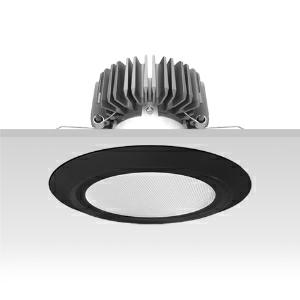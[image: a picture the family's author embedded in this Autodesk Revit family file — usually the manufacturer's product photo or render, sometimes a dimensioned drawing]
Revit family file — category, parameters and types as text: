
# Revit family: 3f_filippi_-_3f_reno_bianco_ampio_3f_filippi_-_30679_a01049_-_3f_reno_200_wh_3000-840_dali_wide___smp_bk_fb56
name_source: partatom
category: Lighting Fixtures
units: mm (PartAtom-declared; Revit-internal decimal feet)

## family parameters
Cut with Voids When Loaded = No
Host = Face
Light Source = No
Part Type = Normal
Room Calculation Point = No
Round Connector Dimension = Use Diameter
Shared = No

## types (1)
- 3F Filippi - 3F Reno Bianco Ampio (1 x LED, 2312 lm, 28 W, 4000 K)
    Apparent Load = 28 VA
    Approval mark = CE
    CIE Flux Codes = 74 92 98 100 100
    Color Rendering = 80
    Color Temperature = 4000 K
    Control Gear = Electronic transformer
    Default Elevation = 1800 mm
    Description = ILLUMINOTECHNICAL
Luminous efficiency 100% (DLOR 100%, ULOR 0%).
Initial luminous flux of the luminaire 2312 lm.
Direct symmetric wide distribution.
Installation Interdistance Transv.D = 1.06 x hu - Long.D = 1.04 x hu.
Tabular UGR (CIE 117 - 4H-8H; S=0.25H; 70/50/20): RUG 22.5 - 22.3.
Beam angle: 70° - 69°.
Luminous efficacy 83 lm/W.
Lifetime (L90/B10): 30000 h. (tq+25°C)
Lifetime (L85/B10): 50000 h. (tq+25°C)
Lifetime (L70/B10): 80000 h. (tq+25°C)
Sudden decreased luminous flux after 50000 hours: 0% (C0).
Photobiological safety in compliance with IEC/TR 62778: RG0 risk exempt, (IEC 62471).
In compliance with IEC/EN 62722-2-1 - IEC/EN 62717 standards.

SOURCE
Compact LED module 3000/840.
Energy efficiency class (UE 2019/2020 - UE 2019/2015): E.
CIE 13.3 Colour rendering index: CRI >80 (R9 <50%).
IES TM-30 Fidelity Index: Rf = 84 Rg = 95.
CCT nominal colour temperature 4000 K.
Colour initial tolerance (MacAdam): SDCM 3.
Zhaga Book 3 compliant.

MECHANICAL
Passive heat dissipator in die-casting aluminium, oversized, for optimum thermal management of the LED module.
Parabolic element with graduated/concentric rings in white polycarbonate.
Transparent external lens with glossy and satin differentiated surfaces, with a cooling and anti-insect system in methacrylate (PMMA).
Fastening spring clips in stainless steel.
Dimensions: diameter 226 mm, height 146 mm. Weight 1.695 kg.
IP44 protection degree for exposed part, IP20 for recessed part.
Mechanical strength to impacts IK05 (0.7 joule).
Glow-wire test resistance 650°C.

ELECTRICAL
Wiring on a separate unit.
Halogen Free DALI-2 DATI (Parts 251, 252, 253), PUSH-DIM, electronic wiring 230V-50/60Hz, power factor 0.97 at full load, THD <25%, constant output current, SELV, class II, 1 driver, 1 DALI addresse.
Power of the luminaire 28 W.
ENEC - CE.
SAFE FLICKER: PstLM=<1 and SVM=<0.4 (IEC TR 61547-1 and IEC TR 63158), to ensure a more comfortable and safe light.
Luminaire compliant with EN 60598-2-22 for power supply from a centralised emergency system CPSS (Central Power Supply System), not incorporated in the luminaire - high risk areas excluded. The default power and flux are 100% in AC and 100% in DC.
Ambient temperature from 0°C to +25°C.
Temperature class T6 max 85°C.
Relative humidity UR: <85%.

INSTALLATION
Pull-up recessed fitting.
False ceiling carving: 200 mm.
All accessories dedicated to this product are available on the Catalog and on our website www.3F-Filippi.com.

ACCESSORIES
A01049 - Anti-glare microprismatic SMP diffuser in methacrylate (PMMA), locked and in line with the trim, in black polycarbonate.

APPLICATIONS
Suitable product for food production plants (HACCP), IFS (Food Version 6), BRC (GSFS Food Version 7).
Environments: architectural, commercial, exhibition areas, transit areas, corridors, shops, display windows, service areas.
In false ceilings with narrow voids.

LIGHT MANAGEMENT
Recommended minimum setting: 10%.
The luminaire, equipped with (DALI-2 DATI) driver, can be controlled manually with 3F Easy Dim technology or automatically/manually with wired or wireless DALI/D2D control systems.
The D2D driver guarantees interoperability with other devices with the same certification by making the following information available:
Device Data (Part 251), Energy Report (Part 252), Diagnosis & Maintenance (Part 253).
In electrical systems without a regulation system (manual or automatic) and DALI bus, a suitable jumper must be made on the DA-DA terminals of the appliance.

WARNING
Luminaire designed for disposal/recycling at end-of-life.
Replaceable (LED only) light source by a professional. Replaceable control gear by a professional.
    Height = 0 mm  [stored 0 ft]
    Lamp = 1 x LED
    Lamp Light Flux = 2312 lm
    Lamp Power = 28 W
    Lamp count = 1
    Length = 226 mm
    Lifetime = 50000 h
    Luminous efficacy = 83 lm/W
    Manufacturer = 3F Filippi
    ModVariant = No
    Model = 3F Filippi - 30679+A01049 - 3F Reno 200 WH 3000-840 DALI WIDE + SMP BK
    Mounting Place = Ceiling
    Mounting Type = Recessed
    Number of Poles = 1
    OnlyDefault = Yes
    Power Factor = 1
    Product Name = 3F Filippi - 3F Reno Bianco Ampio
    Product group = recessed luminaire
    ProductGroupID = 4
    Protection Class = Protection class II
    Protection Degree = IP 20
    RLX_Detail_Level = 1
    RLX_Emergency_Light_Flux = 0 lm
    RLX_Emergency_Type = 0
    RLX_Emergency_Type_DB = No
    RlxData = <blob elided: 99465 chars, md5=6a8d638a>
    Socket = socket
    Standby Power = 0 W
    System Light Flux = 2312 lm
    System Power = 28 W
    Type Comments = Product without accessories
    Type Image = 3ffilippi_3f_reno_200_bk_vs_smp.jpg
    URL = http://relux.com
    VarID = ---
    Voltage = 0 V
    Weight = 0.00 kg
    Width = 0 mm  [stored 0 ft]

note: [stored X ft] marks values corroborated as IEEE doubles in the binary element streams (Revit-internal decimal feet)

## geometry (parser evidence)
native form markers: Blend x4, Sweep x10
no freeform markers — native parametric forms only
